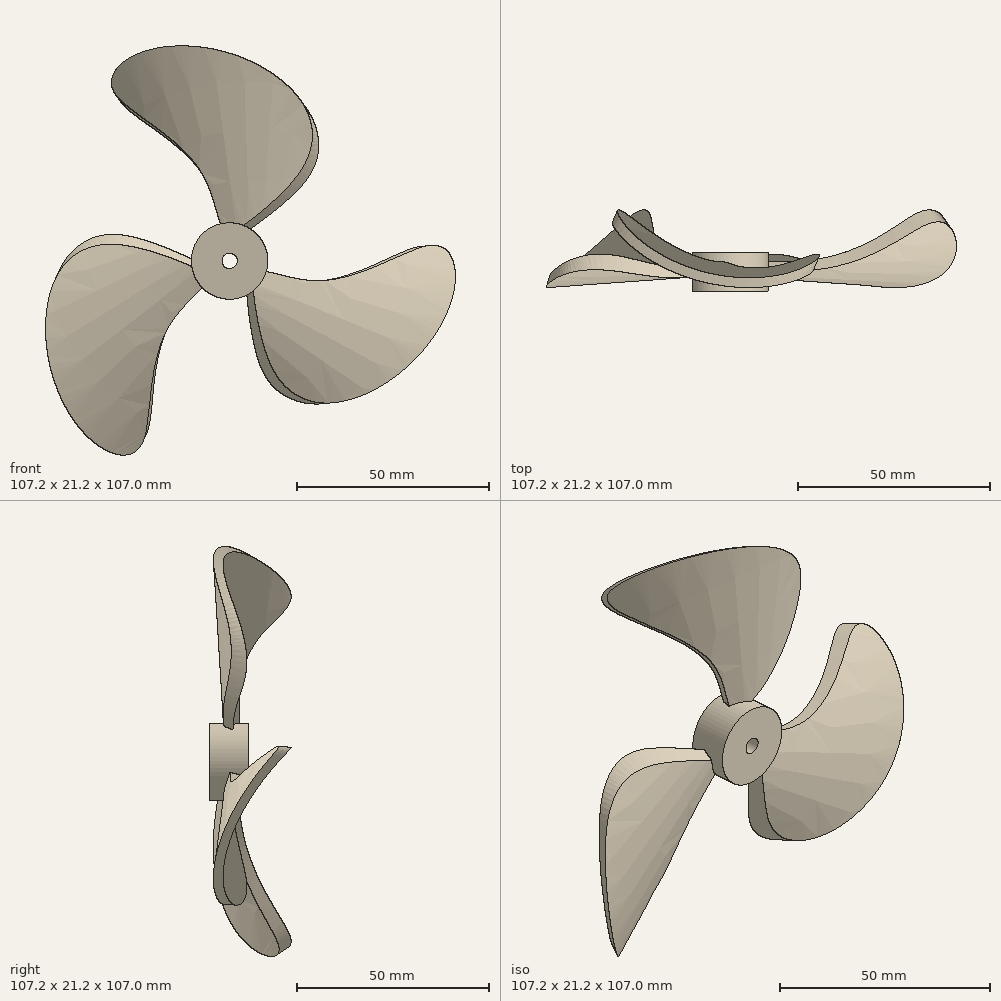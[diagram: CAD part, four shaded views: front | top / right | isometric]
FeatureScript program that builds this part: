
annotation { "Feature Type Name" : "Feature", "Feature Type Description" : "" }
export const myFeature = defineFeature(function(context is Context, id is Id, definition is map)
    precondition{}
    {
        {
            var Q0;
            Q0=qCreatedBy(makeId("Front.planeOp"),FACE);
            var sketch = newSketch(context, id + "F0", { "sketchPlane" : qUnion([Q0])});
            skCircle(sketch, "E0", {"center": v(0, 0) * mm, "radius": 10 * mm});
            skSolve(sketch);
        }
        {
            var Q0;
            Q0 = qSketchRegion(id + "F0", true);
            extrude(context, id + "F1", {"entities" : qUnion([Q0]), "depth" : 5 * mm, "hasSecondDirection" : true, "secondDirectionOppositeDirection" : true, "secondDirectionDepth" : 5 * mm});
        }
        {
            var Q0;
            Q0=qCreatedBy(makeId("Front.planeOp"),FACE);
            var sketch = newSketch(context, id + "F2", { "sketchPlane" : qUnion([Q0])});
            skLineSegment(sketch, "E1", {"start": v(0, 0) * mm, "end": v(0, 100) * mm});
            skLineSegment(sketch, "E2", {"start": v(0, 100) * mm, "end": v(66.33, 100) * mm});
            skLineSegment(sketch, "E3", {"start": v(66.33, 100) * mm, "end": v(0, 0) * mm});
            skSolve(sketch);
        }
        {
            var Q0;
            Q0=makeQuery(id+"F2.imprint","IMPRINT",FACE,{"disambiguationData":[TD([[makeQuery(id+"F2.imprint","IMPRINT",EDGE,{"derivedFrom":sQuery(id+"F2.wireOp",EDGE,"E1")}),-1.0]])]});
            var Q1;
            Q1=sQuery(id+"F2.wireOp",EDGE,"E1");
            revolve(context, id + "F3", {"entities" : qUnion([Q0]), "axis" : qUnion([Q1]), "revolveType" : RevolveType.FULL});
        }
        {
            var Q0;
            Q0=makeQuery(id+"F3.opRevolve","SWEPT_FACE",FACE,{"disambiguationData":[OSD([sQuery(id+"F2.wireOp",EDGE,"E2")])]});
            shell(context, id + "F4", {"entities" : qUnion([Q0]), "thickness" : 2.5 * mm});
        }
        {
            var Q0;
            Q0=qCreatedBy(makeId("Front.planeOp"),FACE);
            var sketch = newSketch(context, id + "F5", { "sketchPlane" : qUnion([Q0])});
            skFitSpline(sketch, "E4", {"points": [v(0, 0) * mm, v(24.24, 27.8) * mm, v(-26.02, 41.1) * mm, v(-4.95, 14.5) * mm, v(0, 0) * mm]});
            skSolve(sketch);
        }
        {
            var Q0;
            Q0 = qSketchRegion(id + "F5", true);
            extrude(context, id + "F6", {"entities" : qUnion([Q0]), "depth" : 50 * mm});
        }
        {
            var Q0;
            Q0=makeQuery(id+"F3.opRevolve","SWEPT_BODY",BODY,{"disambiguationData":[OSD([sQuery(id+"F2.wireOp",EDGE,"E1"),sQuery(id+"F2.wireOp",EDGE,"E2"),sQuery(id+"F2.wireOp",EDGE,"E3")])]});
            var Q1;
            Q1=qCreatedBy(makeId("Origin.pointOp"),VERTEX);
            transform(context, id + "F7", {"entities" : qUnion([Q0]), "transformType" : TransformType.TRANSLATION_3D, "dx" : 0 * mm, "dy" : 0 * mm, "dz" : -26.9 * mm, "makeCopy" : false});
        }
        {
            var Q0;
            Q0=makeQuery(id+"F3.opRevolve","SWEPT_BODY",BODY,{"disambiguationData":[OSD([sQuery(id+"F2.wireOp",EDGE,"E1"),sQuery(id+"F2.wireOp",EDGE,"E2"),sQuery(id+"F2.wireOp",EDGE,"E3")])]});
            var Q1;
            Q1=makeQuery(id+"F6.opExtrude","SWEPT_BODY",BODY,{"disambiguationData":[OSD([sQuery(id+"F5.wireOp",EDGE,"E4")])]});
            booleanBodies(context, id + "F8", {"operationType" : BooleanOperationType.INTERSECTION, "tools" : qUnion([Q0, Q1])});
        }
        {
            var Q0;
            Q0=makeQuery(id+"F8.opBoolean","INTERSECT",BODY,{"derivedFrom":[makeQuery(id+"F3.opRevolve","SWEPT_BODY",BODY,{"disambiguationData":[OSD([sQuery(id+"F2.wireOp",EDGE,"E1"),sQuery(id+"F2.wireOp",EDGE,"E2"),sQuery(id+"F2.wireOp",EDGE,"E3")])]}),makeQuery(id+"F6.opExtrude","SWEPT_BODY",BODY,{"disambiguationData":[OSD([sQuery(id+"F5.wireOp",EDGE,"E4")])]})]});
            transform(context, id + "F9", {"entities" : qUnion([Q0]), "transformType" : TransformType.TRANSLATION_3D, "dx" : 0 * mm, "dy" : 18.2 * mm, "dz" : 6.8 * mm, "makeCopy" : false});
        }
        {
            var Q0;
            Q0=qCreatedBy(makeId("Front.planeOp"),FACE);
            var sketch = newSketch(context, id + "F10", { "sketchPlane" : qUnion([Q0])});
            skLineSegment(sketch, "E5", {"start": v(0, 0) * mm, "end": v(0, 12) * mm, "construction": true});
            skSolve(sketch);
        }
        {
            var Q0;
            Q0=makeQuery(id+"F8.opBoolean","INTERSECT",BODY,{"derivedFrom":[makeQuery(id+"F3.opRevolve","SWEPT_BODY",BODY,{"disambiguationData":[OSD([sQuery(id+"F2.wireOp",EDGE,"E1"),sQuery(id+"F2.wireOp",EDGE,"E2"),sQuery(id+"F2.wireOp",EDGE,"E3")])]}),makeQuery(id+"F6.opExtrude","SWEPT_BODY",BODY,{"disambiguationData":[OSD([sQuery(id+"F5.wireOp",EDGE,"E4")])]})]});
            var Q1;
            Q1=sQuery(id+"F10.wireOp",EDGE,"E5");
            transform(context, id + "F11", {"entities" : qUnion([Q0]), "transformType" : TransformType.ROTATION, "transformAxis" : qUnion([Q1]), "angle" : 20 * degree, "oppositeDirection" : true, "makeCopy" : false});
        }
        {
            var Q0;
            Q0=qCreatedBy(makeId("Front.planeOp"),FACE);
            var sketch = newSketch(context, id + "F12", { "sketchPlane" : qUnion([Q0])});
            skLineSegment(sketch, "E6", {"start": v(0, 0) * mm, "end": v(-20, 0) * mm, "construction": true});
            skSolve(sketch);
        }
        {
            var Q0;
            Q0=makeQuery(id+"F8.opBoolean","INTERSECT",BODY,{"derivedFrom":[makeQuery(id+"F3.opRevolve","SWEPT_BODY",BODY,{"disambiguationData":[OSD([sQuery(id+"F2.wireOp",EDGE,"E1"),sQuery(id+"F2.wireOp",EDGE,"E2"),sQuery(id+"F2.wireOp",EDGE,"E3")])]}),makeQuery(id+"F6.opExtrude","SWEPT_BODY",BODY,{"disambiguationData":[OSD([sQuery(id+"F5.wireOp",EDGE,"E4")])]})]});
            var Q1;
            Q1=sQuery(id+"F12.wireOp",EDGE,"E6");
            transform(context, id + "F13", {"entities" : qUnion([Q0]), "transformType" : TransformType.ROTATION, "transformAxis" : qUnion([Q1]), "angle" : 30 * degree, "makeCopy" : false});
        }
        {
            var Q0;
            Q0=makeQuery(id+"F8.opBoolean","INTERSECT",BODY,{"derivedFrom":[makeQuery(id+"F3.opRevolve","SWEPT_BODY",BODY,{"disambiguationData":[OSD([sQuery(id+"F2.wireOp",EDGE,"E1"),sQuery(id+"F2.wireOp",EDGE,"E2"),sQuery(id+"F2.wireOp",EDGE,"E3")])]}),makeQuery(id+"F6.opExtrude","SWEPT_BODY",BODY,{"disambiguationData":[OSD([sQuery(id+"F5.wireOp",EDGE,"E4")])]})]});
            transform(context, id + "F14", {"entities" : qUnion([Q0]), "transformType" : TransformType.TRANSLATION_3D, "dx" : 0 * mm, "dy" : -4.1 * mm, "dz" : 1.8 * mm, "makeCopy" : false});
        }
        {
            var Q0;
            Q0=makeQuery(id+"F8.opBoolean","INTERSECT",BODY,{"derivedFrom":[makeQuery(id+"F3.opRevolve","SWEPT_BODY",BODY,{"disambiguationData":[OSD([sQuery(id+"F2.wireOp",EDGE,"E1"),sQuery(id+"F2.wireOp",EDGE,"E2"),sQuery(id+"F2.wireOp",EDGE,"E3")])]}),makeQuery(id+"F6.opExtrude","SWEPT_BODY",BODY,{"disambiguationData":[OSD([sQuery(id+"F5.wireOp",EDGE,"E4")])]})]});
            var Q1;
            Q1=makeQuery(id+"F1.opExtrude","CAP_EDGE",EDGE,{"disambiguationData":[OSD([sQuery(id+"F0.wireOp",EDGE,"E0")])],"isStart":false});
            circularPattern(context, id + "F15", {"entities" : qUnion([Q0]), "axis" : qUnion([Q1]), "angle" : 360 * degree, "instanceCount" : 3, "equalSpace" : true});
        }
        {
            var Q0;
            Q0=makeQuery(id+"F1.opExtrude","CAP_FACE",FACE,{"disambiguationData":[OSD([sQuery(id+"F0.wireOp",EDGE,"E0")])],"isStart":false});
            var sketch = newSketch(context, id + "F16", { "sketchPlane" : qUnion([Q0])});
            skCircle(sketch, "E7", {"center": v(0, 0) * mm, "radius": 2 * mm});
            skSolve(sketch);
        }
        {
            var Q0;
            Q0 = qSketchRegion(id + "F16", true);
            var Q1;
            Q1=makeQuery(id+"F1.opExtrude","CAP_FACE",FACE,{"disambiguationData":[OSD([sQuery(id+"F0.wireOp",EDGE,"E0")])],"isStart":true});
            extrude(context, id + "F17", {"entities" : qUnion([Q0]), "operationType" : NewBodyOperationType.REMOVE, "endBound" : BoundingType.UP_TO_SURFACE, "oppositeDirection" : true, "endBoundEntityFace" : qUnion([Q1]), "depth" : 25 * mm});
        }
    });
